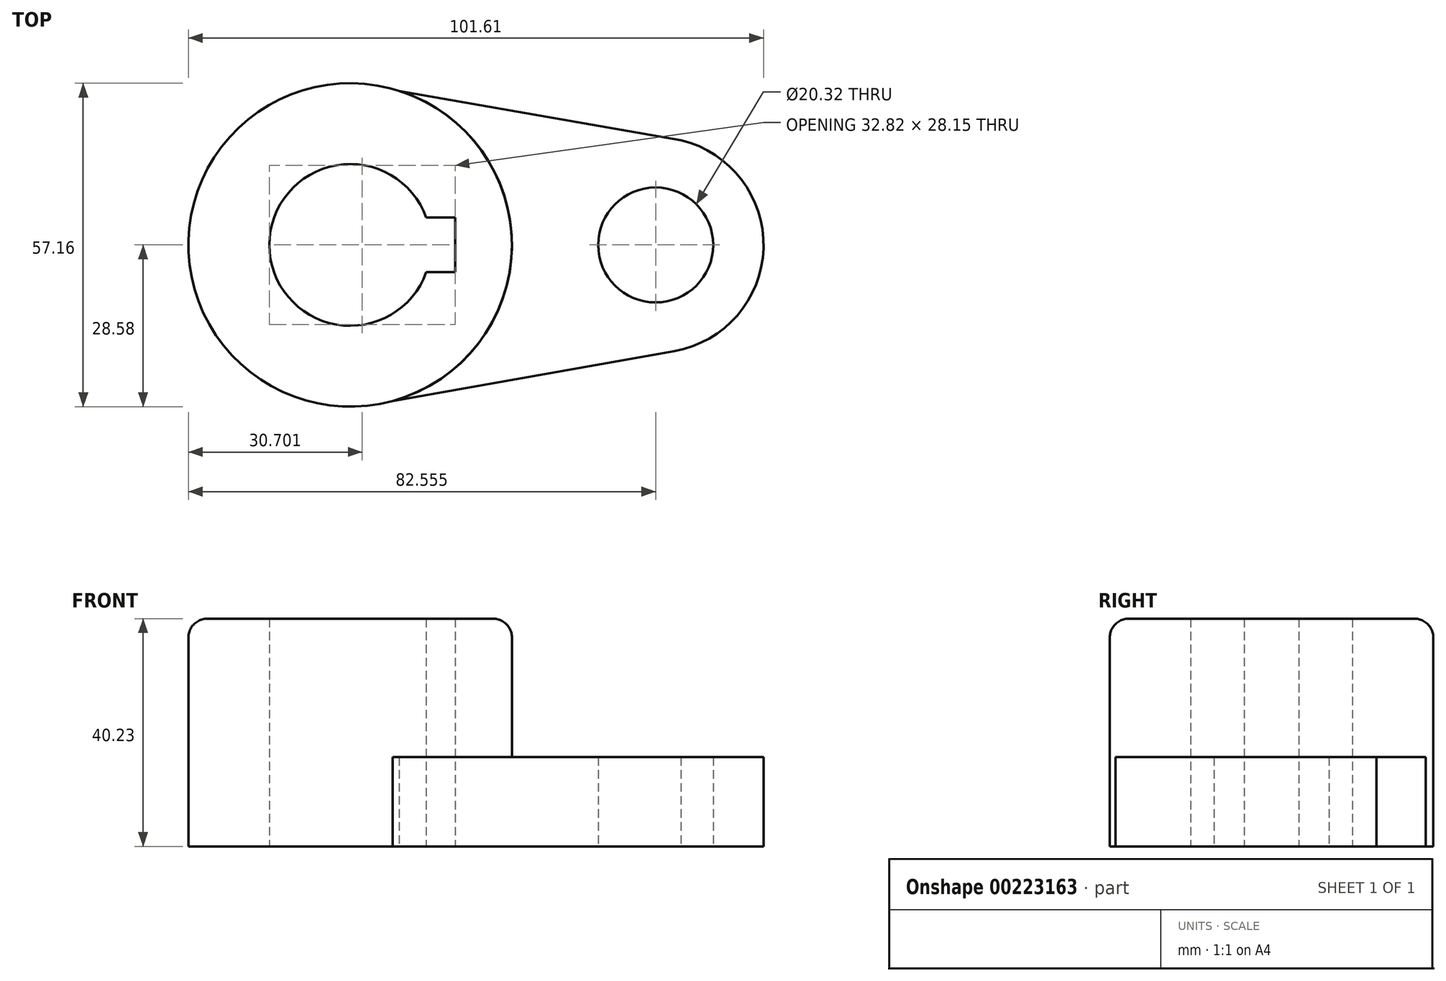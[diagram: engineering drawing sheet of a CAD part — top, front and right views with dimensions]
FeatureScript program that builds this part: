
annotation { "Feature Type Name" : "Feature", "Feature Type Description" : "" }
export const myFeature = defineFeature(function(context is Context, id is Id, definition is map)
    precondition{}
    {
        {
            var Q0;
            Q0=qCreatedBy(makeId("Top.planeOp"),FACE);
            var sketch = newSketch(context, id + "F0", { "sketchPlane" : qUnion([Q0])});
            skCircle(sketch, "E0", {"center": v(0, 0) * mm, "radius": 28.58 * mm});
            skCircle(sketch, "E1", {"center": v(53.98, 0) * mm, "radius": 10.16 * mm});
            skArc(sketch, "E2", {"start": v(13.45, 4.83) * mm, "mid": v(-14.29, 0) * mm, "end": v(13.45, -4.83) * mm});
            skLineSegment(sketch, "E3.bottom", {"start": v(18.53, 4.83) * mm, "end": v(13.45, 4.83) * mm});
            skLineSegment(sketch, "E3.top", {"start": v(18.53, -4.83) * mm, "end": v(13.45, -4.83) * mm});
            skLineSegment(sketch, "E3.left", {"start": v(18.53, 4.83) * mm, "end": v(18.53, -4.83) * mm});
            skPoint(sketch, "E4.end.orphan", {"position": v(-14.29, 0) * mm});
            skPoint(sketch, "E3.right.end.orphan", {"position": v(-18.53, -4.83) * mm});
            skPoint(sketch, "E5.trimOffspring.end.orphan", {"position": v(-18.53, 4.83) * mm});
            skCircle(sketch, "E6", {"center": v(53.98, 0) * mm, "radius": 19.05 * mm});
            skLineSegment(sketch, "E7", {"start": v(8.65, 27.23) * mm, "end": v(58.44, 18.52) * mm});
            skLineSegment(sketch, "E8", {"start": v(7.52, -27.57) * mm, "end": v(57.3, -18.76) * mm});
            skSolve(sketch);
        }
        {
            var Q0;
            {var subQ3=sQuery(id+"F0.wireOp",EDGE,"E8");Q0=makeQuery(id+"F0.imprint","IMPRINT",FACE,{"disambiguationData":[TD([[makeQuery(id+"F0.imprint","IMPRINT",EDGE,{"derivedFrom":subQ3}),1.0]])]});}
            var Q1;
            Q1=makeQuery(id+"F0.imprint","IMPRINT",FACE,{"disambiguationData":[TD([[makeQuery(id+"F0.imprint","IMPRINT",EDGE,{"derivedFrom":sQuery(id+"F0.wireOp",EDGE,"E1")}),-1.0]])]});
            extrude(context, id + "F1", {"entities" : qUnion([Q0, Q1]), "depth" : 15.77 * mm});
        }
        {
            var Q0;
            Q0=qCreatedBy(makeId("Top.planeOp"),FACE);
            var sketch = newSketch(context, id + "F2", { "sketchPlane" : qUnion([Q0])});
            skCircle(sketch, "E9.0", {"center": v(0, 0) * mm, "radius": 28.58 * mm});
            skCircle(sketch, "E9.1", {"center": v(53.98, 0) * mm, "radius": 10.16 * mm});
            skArc(sketch, "E9.2", {"start": v(13.45, 4.83) * mm, "mid": v(-14.29, 0) * mm, "end": v(13.45, -4.83) * mm});
            skLineSegment(sketch, "E9.3", {"start": v(18.53, 4.83) * mm, "end": v(13.45, 4.83) * mm});
            skLineSegment(sketch, "E9.4", {"start": v(18.53, -4.83) * mm, "end": v(13.45, -4.83) * mm});
            skLineSegment(sketch, "E9.5", {"start": v(18.53, 4.83) * mm, "end": v(18.53, -4.83) * mm});
            skPoint(sketch, "E9.6", {"position": v(0, 0) * mm});
            skPoint(sketch, "E9.7", {"position": v(-14.29, 0) * mm});
            skPoint(sketch, "E9.8", {"position": v(-18.53, -4.83) * mm});
            skPoint(sketch, "E9.9", {"position": v(-18.53, 4.83) * mm});
            skCircle(sketch, "E9.10", {"center": v(53.98, 0) * mm, "radius": 19.05 * mm});
            skLineSegment(sketch, "E9.11", {"start": v(8.65, 27.23) * mm, "end": v(58.44, 18.52) * mm});
            skLineSegment(sketch, "E9.12", {"start": v(7.52, -27.57) * mm, "end": v(57.3, -18.76) * mm});
            skSolve(sketch);
        }
        {
            var Q0;
            Q0=makeQuery(id+"F2.imprint","IMPRINT",FACE,{"disambiguationData":[TD([[makeQuery(id+"F2.imprint","IMPRINT",EDGE,{"derivedFrom":sQuery(id+"F2.wireOp",EDGE,"E9.2")}),-1.0]])]});
            extrude(context, id + "F3", {"entities" : qUnion([Q0]), "operationType" : NewBodyOperationType.ADD, "depth" : 40.23 * mm});
        }
        {
            var Q0;
            Q0=makeQuery(id+"F3.opExtrude","CAP_EDGE",EDGE,{"disambiguationData":[OSD([sQuery(id+"F2.wireOp",EDGE,"E9.0")])],"isStart":false});
            fillet(context, id + "F4", {"entities" : qUnion([Q0]), "radius" : 3.3 * mm, "tangentPropagation" : true, "allowEdgeOverflow" : false});
        }
    });
